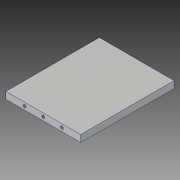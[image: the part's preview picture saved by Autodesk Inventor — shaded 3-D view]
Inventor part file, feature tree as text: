
AUTODESK INVENTOR PART (.ipt)
format: ipt  version: 2019 (Build 230136000, 136)  size: 96,256 bytes
history: native  units: mm
features: sketch x3, hole x2, extrude x1
ambient origin geometry x8: Origin, YZ Plane, XZ Plane, XY Plane, X Axis, Y Axis, Z Axis, Center Point
bodies: Solid1 (feature_tree)
feature tree (6):
  extrude  "Extrusion1"  Depth=135.0mm
  hole  "Hole1"  [1 undecoded]
  hole  "Hole2"  [1 undecoded]
  sketch  "Sketch1"  dims[d0=108.0mm d1=135.0mm]
  sketch  "Sketch2"  dims[d2=10.0mm d3=0.0mm d4=54.0mm]
  sketch  "Sketch3"  dims[d5=4.134mm d6=12.0mm d7=4.0mm d8=2.0mm d9=90.0deg d10=14.2mm d11=20.594885mm d12=4.134mm d13=12.0mm d14=4.0mm d15=2.0mm d16=90.0deg d17=14.2mm d18=20.594885mm]
note: 2 required parameter values undecoded (feature->parameter linkage not recoverable at this tier; creation-order binding heuristic only, values carry confidence <= 0.55)
